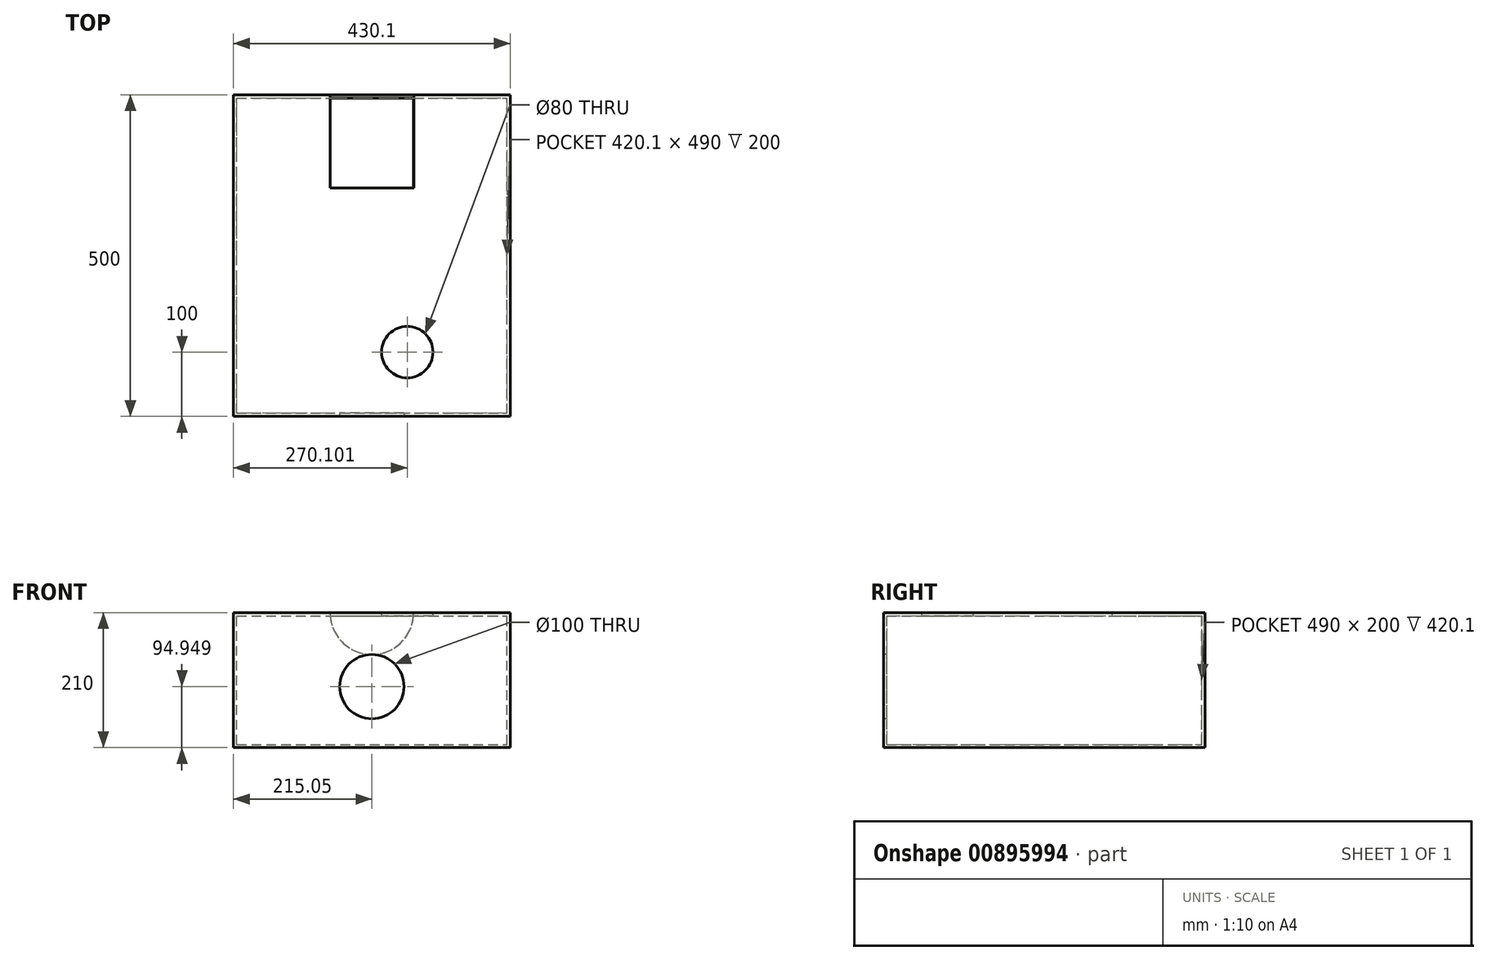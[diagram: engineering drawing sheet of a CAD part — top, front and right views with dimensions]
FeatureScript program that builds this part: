
annotation { "Feature Type Name" : "Feature", "Feature Type Description" : "" }
export const myFeature = defineFeature(function(context is Context, id is Id, definition is map)
    precondition{}
    {
        {
            var Q0;
            Q0=qCreatedBy(makeId("Front.planeOp"),FACE);
            var sketch = newSketch(context, id + "F0", { "sketchPlane" : qUnion([Q0])});
            skLineSegment(sketch, "E0.bottom", {"start": v(-133.8, -172.68) * mm, "end": v(296.3, -172.68) * mm});
            skLineSegment(sketch, "E0.top", {"start": v(-133.8, 37.32) * mm, "end": v(16.2, 37.32) * mm});
            skLineSegment(sketch, "E0.left", {"start": v(-133.8, -172.68) * mm, "end": v(-133.8, 37.32) * mm});
            skLineSegment(sketch, "E0.right", {"start": v(296.3, -172.68) * mm, "end": v(296.3, 37.32) * mm});
            skLineSegment(sketch, "E1.trimOffspring", {"start": v(146.3, 37.32) * mm, "end": v(296.3, 37.32) * mm});
            skArc(sketch, "E2", {"start": v(16.2, 37.32) * mm, "mid": v(81.25, -27.73) * mm, "end": v(146.3, 37.32) * mm});
            skSolve(sketch);
        }
        {
            var Q0;
            Q0 = qSketchRegion(id + "F0", true);
            extrude(context, id + "F1", {"entities" : qUnion([Q0]), "depth" : 500 * mm, "offsetDistance" : 25 * mm});
        }
        {
            var Q0;
            Q0=makeQuery(id+"F1.opExtrude","SWEPT_FACE",FACE,{"disambiguationData":[OSD([sQuery(id+"F0.wireOp",EDGE,"2p9MXA8n-5yLB-3Tbz-tV5X-GLF00WAAFGTN")])]});
            var Q1;
            Q1=makeQuery(id+"F1.opExtrude","SWEPT_FACE",FACE,{"disambiguationData":[OSD([sQuery(id+"F0.wireOp",EDGE,"dW43V3MA-0CpX-7ZK2-8CGb-Xv0E1A18Es13")])]});
            var Q2;
            Q2=makeQuery(id+"F1.opExtrude","SWEPT_FACE",FACE,{"disambiguationData":[OSD([sQuery(id+"F0.wireOp",EDGE,"U2EUXn2e-wvPi-WCaP-VYMh-x3uaRrqhHojm")])]});
            var Q3;
            Q3=makeQuery(id+"F1.opExtrude","SWEPT_FACE",FACE,{"disambiguationData":[OSD([sQuery(id+"F0.wireOp",EDGE,"E2")])]});
            shell(context, id + "F2", {"entities" : qUnion([Q0, Q1, Q2, Q3]), "thickness" : 5 * mm});
        }
        {
            var Q0;
            Q0=makeQuery(id+"F1.opExtrude","CAP_FACE",FACE,{"disambiguationData":[OSD([sQuery(id+"F0.wireOp",EDGE,"E0.bottom"),sQuery(id+"F0.wireOp",EDGE,"E0.top"),sQuery(id+"F0.wireOp",EDGE,"E0.left"),sQuery(id+"F0.wireOp",EDGE,"E0.right"),sQuery(id+"F0.wireOp",EDGE,"E1.trimOffspring"),sQuery(id+"F0.wireOp",EDGE,"E2")])],"isStart":false});
            var sketch = newSketch(context, id + "F3", { "sketchPlane" : qUnion([Q0])});
            skLineSegment(sketch, "E3", {"start": v(16.2, 37.32) * mm, "end": v(146.3, 37.32) * mm});
            skCircle(sketch, "E4", {"center": v(81.25, -77.73) * mm, "radius": 50 * mm});
            skLineSegment(sketch, "E5", {"start": v(81.25, -27.73) * mm, "end": v(81.25, -27.73) * mm});
            skLineSegment(sketch, "E6", {"start": v(81.25, -77.73) * mm, "end": v(81.25, -27.73) * mm});
            skSolve(sketch);
        }
        {
            var Q0;
            Q0=makeQuery(id+"F3.imprint","IMPRINT",FACE,{"disambiguationData":[TD([[makeQuery(id+"F3.imprint","IMPRINT",EDGE,{"derivedFrom":sQuery(id+"F3.wireOp",EDGE,"E3")}),-1.0]])]});
            extrude(context, id + "F4", {"entities" : qUnion([Q0]), "operationType" : NewBodyOperationType.ADD, "depth" : -5 * mm, "offsetDistance" : 25 * mm});
        }
        {
            var Q0;
            Q0 = qSketchRegion(id + "F3", true);
            extrude(context, id + "F5", {"entities" : qUnion([Q0]), "operationType" : NewBodyOperationType.REMOVE, "depth" : -10 * mm, "offsetDistance" : 25 * mm});
        }
        {
            var Q0;
            Q0=makeQuery(id+"F4.boolean.opBoolean","MERGE",FACE,{"derivedFrom":[makeQuery(id+"F1.opExtrude","SWEPT_FACE",FACE,{"disambiguationData":[OSD([sQuery(id+"F0.wireOp",EDGE,"E0.top")])]}),makeQuery(id+"F1.opExtrude","SWEPT_FACE",FACE,{"disambiguationData":[OSD([sQuery(id+"F0.wireOp",EDGE,"E1.trimOffspring")])]}),makeQuery(id+"F4.opExtrude","SWEPT_FACE",FACE,{"disambiguationData":[OSD([sQuery(id+"F3.wireOp",EDGE,"E3")])]})]});
            var sketch = newSketch(context, id + "F6", { "sketchPlane" : qUnion([Q0])});
            skLineSegment(sketch, "E7", {"start": v(16.2, -145) * mm, "end": v(146.3, -145) * mm});
            skPoint(sketch, "E7.endSnap0", {"position": v(146.3, -247.5) * mm});
            skSolve(sketch);
        }
        {
            var Q0;
            {var subQ0=sQuery(id+"F6.wireOp",EDGE,"E7");Q0=makeQuery(id+"F6.imprint","IMPRINT",FACE,{"disambiguationData":[TD([[makeQuery(id+"F6.imprint","IMPRINT",EDGE,{"derivedFrom":subQ0}),-1.0]])]});}
            extrude(context, id + "F7", {"entities" : qUnion([Q0]), "operationType" : NewBodyOperationType.ADD, "depth" : -5 * mm, "offsetDistance" : 25 * mm});
        }
        {
            var Q0;
            {var subQ0=sQuery(id+"F3.wireOp",EDGE,"E3");var subQ1=sQuery(id+"F0.wireOp",EDGE,"E1.trimOffspring");var subQ2=sQuery(id+"F0.wireOp",EDGE,"E0.top");Q0=makeQuery(id+"F7.boolean.opBoolean","MERGE",FACE,{"derivedFrom":[makeQuery(id+"F4.boolean.opBoolean","MERGE",FACE,{"derivedFrom":[makeQuery(id+"F1.opExtrude","SWEPT_FACE",FACE,{"disambiguationData":[OSD([subQ2])]}),makeQuery(id+"F1.opExtrude","SWEPT_FACE",FACE,{"disambiguationData":[OSD([subQ1])]}),makeQuery(id+"F4.opExtrude","SWEPT_FACE",FACE,{"disambiguationData":[OSD([subQ0])]})]}),makeQuery(id+"F7.opExtrude","CAP_FACE",FACE,{"disambiguationData":[OSD([subQ2,subQ1,sQuery(id+"F0.wireOp",EDGE,"E2"),subQ0,sQuery(id+"F6.wireOp",EDGE,"E7")])],"isStart":true})]});}
            var sketch = newSketch(context, id + "F8", { "sketchPlane" : qUnion([Q0])});
            skCircle(sketch, "E8", {"center": v(136.3, -400) * mm, "radius": 40 * mm});
            skSolve(sketch);
        }
        {
            var Q0;
            Q0 = qSketchRegion(id + "F8", true);
            extrude(context, id + "F9", {"entities" : qUnion([Q0]), "operationType" : NewBodyOperationType.REMOVE, "oppositeDirection" : true, "depth" : 25 * mm, "offsetDistance" : 25 * mm});
        }
    });
